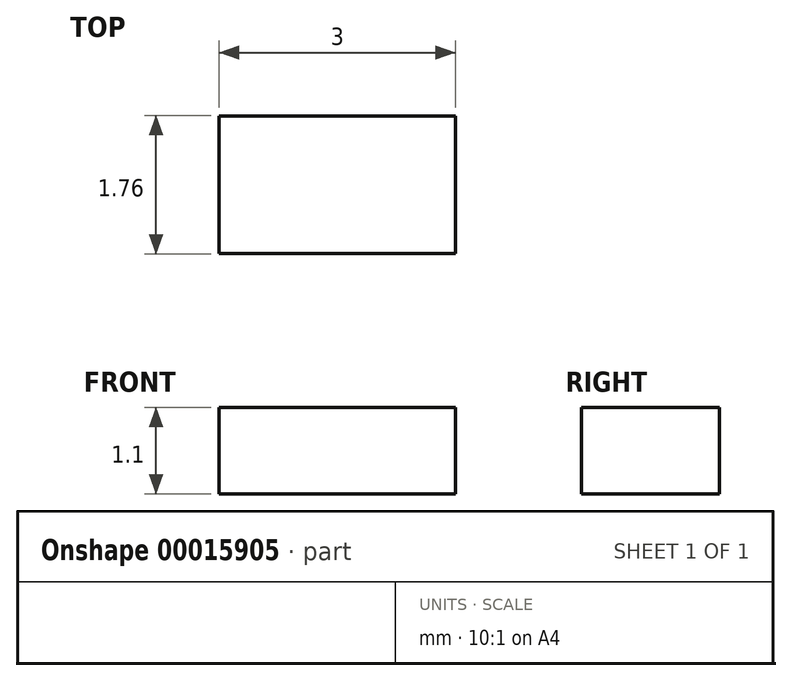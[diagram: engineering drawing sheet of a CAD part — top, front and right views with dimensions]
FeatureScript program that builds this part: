
annotation { "Feature Type Name" : "Feature", "Feature Type Description" : "" }
export const myFeature = defineFeature(function(context is Context, id is Id, definition is map)
    precondition{}
    {
        {
            var Q0;
            Q0=qCreatedBy(makeId("Top.planeOp"),FACE);
            var sketch = newSketch(context, id + "F0", { "sketchPlane" : qUnion([Q0])});
            skLineSegment(sketch, "E0.rect.bottom", {"start": v(1.5, 0.87) * mm, "end": v(-1.5, 0.87) * mm});
            skLineSegment(sketch, "E0.rect.top", {"start": v(1.5, -0.87) * mm, "end": v(-1.5, -0.87) * mm});
            skLineSegment(sketch, "E0.rect.left", {"start": v(1.5, 0.87) * mm, "end": v(1.5, -0.87) * mm});
            skLineSegment(sketch, "E0.rect.right", {"start": v(-1.5, 0.87) * mm, "end": v(-1.5, -0.87) * mm});
            skPoint(sketch, "E0.rect.middle", {"position": v(0, 0) * mm});
            skSolve(sketch);
        }
        {
            var Q0;
            Q0=makeQuery(id+"F0.imprint","IMPRINT",FACE,{"disambiguationData":[TD([[makeQuery(id+"F0.imprint","IMPRINT",EDGE,{"derivedFrom":sQuery(id+"F0.wireOp",EDGE,"E0.rect.bottom")}),1.0]])]});
            extrude(context, id + "F1", {"entities" : qUnion([Q0]), "depth" : 1.1 * mm});
        }
    });
